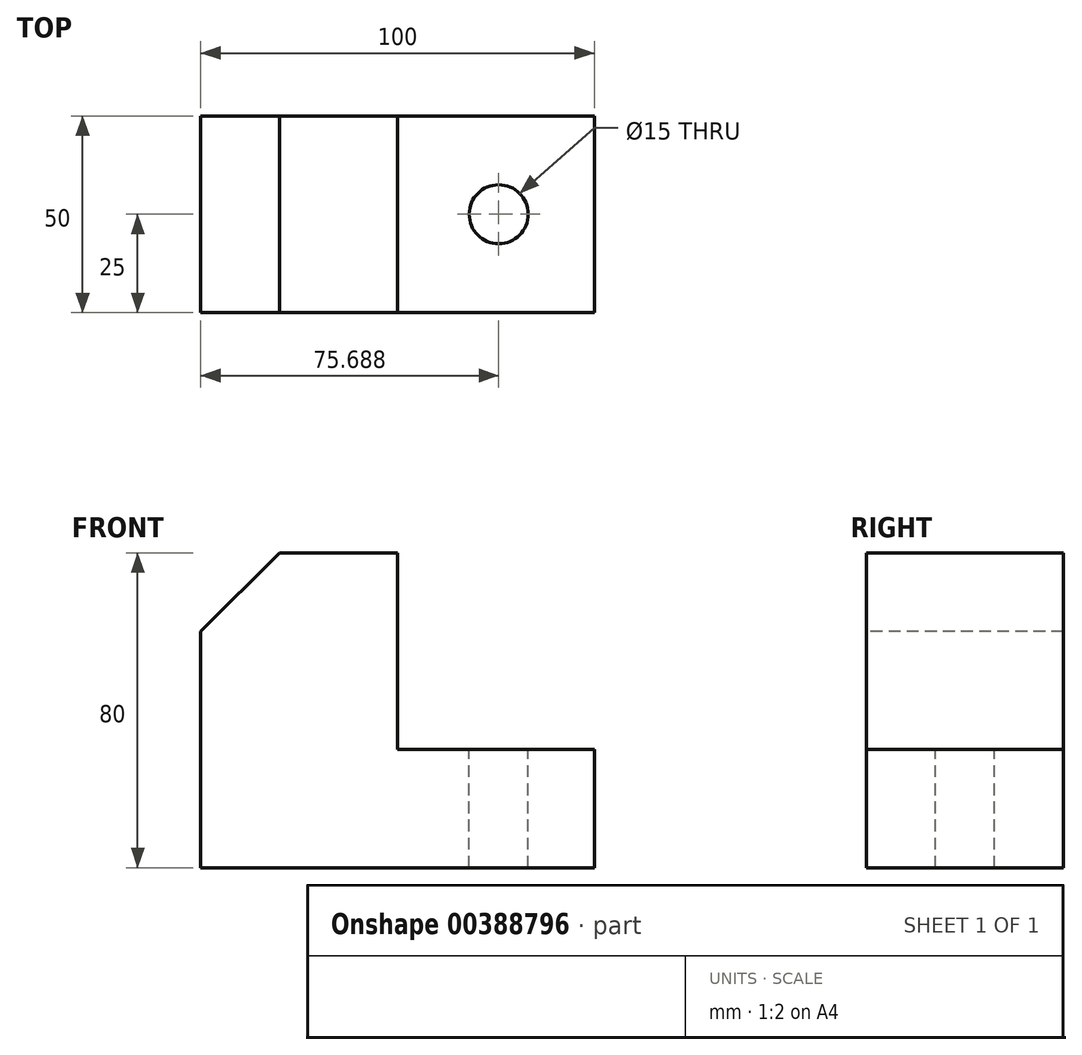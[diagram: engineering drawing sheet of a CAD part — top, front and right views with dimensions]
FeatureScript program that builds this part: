
annotation { "Feature Type Name" : "Feature", "Feature Type Description" : "" }
export const myFeature = defineFeature(function(context is Context, id is Id, definition is map)
    precondition{}
    {
        {
            var Q0;
            Q0=qCreatedBy(makeId("Top.planeOp"),FACE);
            var sketch = newSketch(context, id + "F0", { "sketchPlane" : qUnion([Q0])});
            skLineSegment(sketch, "E0.bottom", {"start": v(0, 0) * mm, "end": v(100, 0) * mm});
            skLineSegment(sketch, "E0.top", {"start": v(0, 50) * mm, "end": v(100, 50) * mm});
            skLineSegment(sketch, "E0.left", {"start": v(0, 0) * mm, "end": v(0, 50) * mm});
            skLineSegment(sketch, "E0.right", {"start": v(100, 0) * mm, "end": v(100, 50) * mm});
            skSolve(sketch);
        }
        {
            var Q0;
            Q0 = qSketchRegion(id + "F0", true);
            extrude(context, id + "F1", {"entities" : qUnion([Q0]), "depth" : 80 * mm});
        }
        {
            var Q0;
            Q0=makeQuery(id+"F1.opExtrude","CAP_FACE",FACE,{"disambiguationData":[OSD([sQuery(id+"F0.wireOp",EDGE,"E0.bottom"),sQuery(id+"F0.wireOp",EDGE,"E0.top"),sQuery(id+"F0.wireOp",EDGE,"E0.left"),sQuery(id+"F0.wireOp",EDGE,"E0.right")])],"isStart":false});
            var sketch = newSketch(context, id + "F2", { "sketchPlane" : qUnion([Q0])});
            skLineSegment(sketch, "E1.bottom", {"start": v(100, 50) * mm, "end": v(50, 50) * mm});
            skLineSegment(sketch, "E1.top", {"start": v(100, 0) * mm, "end": v(50, 0) * mm});
            skLineSegment(sketch, "E1.left", {"start": v(100, 50) * mm, "end": v(100, 0) * mm});
            skLineSegment(sketch, "E1.right", {"start": v(50, 50) * mm, "end": v(50, 0) * mm});
            skSolve(sketch);
        }
        {
            var Q0;
            Q0 = qSketchRegion(id + "F2", true);
            extrude(context, id + "F3", {"entities" : qUnion([Q0]), "operationType" : NewBodyOperationType.REMOVE, "oppositeDirection" : true, "depth" : 50 * mm});
        }
        {
            var Q0;
            Q0=makeQuery(id+"F1.opExtrude","SWEPT_FACE",FACE,{"disambiguationData":[OSD([sQuery(id+"F0.wireOp",EDGE,"E0.bottom")])]});
            var sketch = newSketch(context, id + "F4", { "sketchPlane" : qUnion([Q0])});
            skLineSegment(sketch, "E2", {"start": v(0, 80) * mm, "end": v(20, 80) * mm});
            skLineSegment(sketch, "E3", {"start": v(20, 80) * mm, "end": v(0, 60) * mm});
            skLineSegment(sketch, "E4", {"start": v(0, 60) * mm, "end": v(0, 80) * mm});
            skSolve(sketch);
        }
        {
            var Q0;
            Q0 = qSketchRegion(id + "F4", true);
            var Q1;
            Q1=makeQuery(id+"F1.opExtrude","SWEPT_FACE",FACE,{"disambiguationData":[OSD([sQuery(id+"F0.wireOp",EDGE,"E0.top")])]});
            extrude(context, id + "F5", {"entities" : qUnion([Q0]), "operationType" : NewBodyOperationType.REMOVE, "endBound" : BoundingType.UP_TO_SURFACE, "oppositeDirection" : true, "endBoundEntityFace" : qUnion([Q1]), "depth" : 25 * mm});
        }
        {
            var Q0;
            Q0=makeQuery(id+"F3.boolean.opBoolean","COPY",FACE,{"derivedFrom":makeQuery(id+"F3.opExtrude","CAP_FACE",FACE,{"disambiguationData":[OSD([sQuery(id+"F2.wireOp",EDGE,"E1.bottom"),sQuery(id+"F2.wireOp",EDGE,"E1.top"),sQuery(id+"F2.wireOp",EDGE,"E1.left"),sQuery(id+"F2.wireOp",EDGE,"E1.right")])],"isStart":false})});
            var sketch = newSketch(context, id + "F6", { "sketchPlane" : qUnion([Q0])});
            skCircle(sketch, "E5", {"center": v(75.69, 25) * mm, "radius": 7.5 * mm});
            skSolve(sketch);
        }
        {
            var Q0;
            Q0 = qSketchRegion(id + "F6", true);
            var Q1;
            Q1=makeQuery(id+"F1.opExtrude","CAP_FACE",FACE,{"disambiguationData":[OSD([sQuery(id+"F0.wireOp",EDGE,"E0.bottom"),sQuery(id+"F0.wireOp",EDGE,"E0.top"),sQuery(id+"F0.wireOp",EDGE,"E0.left"),sQuery(id+"F0.wireOp",EDGE,"E0.right")])],"isStart":true});
            extrude(context, id + "F7", {"entities" : qUnion([Q0]), "operationType" : NewBodyOperationType.REMOVE, "endBound" : BoundingType.UP_TO_SURFACE, "oppositeDirection" : true, "endBoundEntityFace" : qUnion([Q1]), "depth" : 25 * mm});
        }
    });
